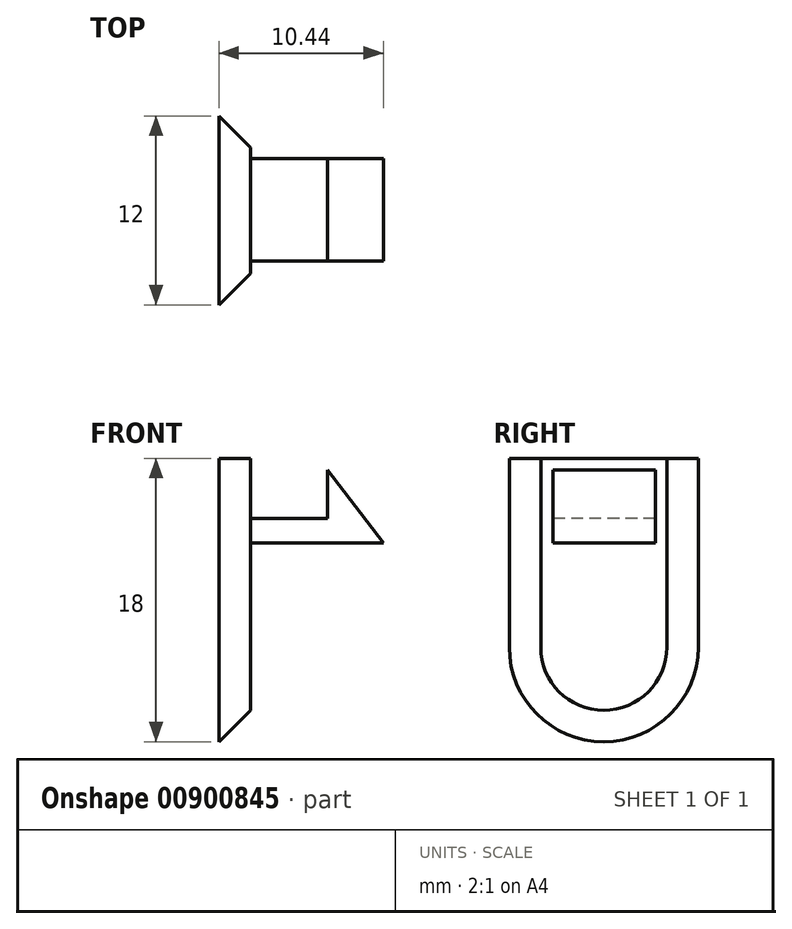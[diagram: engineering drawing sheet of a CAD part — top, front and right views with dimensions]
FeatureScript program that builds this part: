
annotation { "Feature Type Name" : "Feature", "Feature Type Description" : "" }
export const myFeature = defineFeature(function(context is Context, id is Id, definition is map)
    precondition{}
    {
        {
            var Q0;
            Q0=qCreatedBy(makeId("Right.planeOp"),FACE);
            var sketch = newSketch(context, id + "F0", { "sketchPlane" : qUnion([Q0])});
            skLineSegment(sketch, "E0.bottom", {"start": v(6, 9) * mm, "end": v(-6, 9) * mm});
            skLineSegment(sketch, "E0.top", {"start": v(6, -9) * mm, "end": v(-6, -9) * mm});
            skLineSegment(sketch, "E0.left", {"start": v(6, 9) * mm, "end": v(6, -9) * mm});
            skLineSegment(sketch, "E0.right", {"start": v(-6, 9) * mm, "end": v(-6, -9) * mm});
            skPoint(sketch, "E0.middle", {"position": v(0, 0) * mm});
            skLineSegment(sketch, "E1", {"start": v(-45.32, 0) * mm, "end": v(56.37, 0) * mm, "construction": true});
            skLineSegment(sketch, "E2", {"start": v(0, 55.34) * mm, "end": v(0, -57.03) * mm, "construction": true});
            skSolve(sketch);
        }
        {
            var Q0;
            Q0=makeQuery(id+"F0.imprint","IMPRINT",FACE,{"disambiguationData":[TD([[makeQuery(id+"F0.imprint","IMPRINT",EDGE,{"derivedFrom":sQuery(id+"F0.wireOp",EDGE,"E0.bottom")}),1.0]])]});
            extrude(context, id + "F1", {"entities" : qUnion([Q0]), "depth" : 2 * mm, "offsetDistance" : 25 * mm});
        }
        {
            var Q0;
            Q0=makeQuery(id+"F1.opExtrude","CAP_FACE",FACE,{"disambiguationData":[OSD([sQuery(id+"F0.wireOp",EDGE,"E0.bottom"),sQuery(id+"F0.wireOp",EDGE,"E0.top"),sQuery(id+"F0.wireOp",EDGE,"E0.left"),sQuery(id+"F0.wireOp",EDGE,"E0.right")])],"isStart":false});
            var sketch = newSketch(context, id + "F2", { "sketchPlane" : qUnion([Q0])});
            skLineSegment(sketch, "E3.bottom", {"start": v(-4.5, 9) * mm, "end": v(4.5, 9) * mm});
            skLineSegment(sketch, "E3.top", {"start": v(-4.5, -7) * mm, "end": v(4.5, -7) * mm});
            skLineSegment(sketch, "E3.left", {"start": v(-4.5, 9) * mm, "end": v(-4.5, -7) * mm});
            skLineSegment(sketch, "E3.right", {"start": v(4.5, 9) * mm, "end": v(4.5, -7) * mm});
            skSolve(sketch);
        }
        {
            var Q0;
            Q0=makeQuery(id+"F1.opExtrude","SWEPT_EDGE",EDGE,{"disambiguationData":[OSD([sQuery(id+"F0.wireOp",EDGE,"E0.top"),sQuery(id+"F0.wireOp",EDGE,"E0.left")])]});
            var Q1;
            Q1=makeQuery(id+"F1.opExtrude","SWEPT_EDGE",EDGE,{"disambiguationData":[OSD([sQuery(id+"F0.wireOp",EDGE,"E0.top"),sQuery(id+"F0.wireOp",EDGE,"E0.right")])]});
            fillet(context, id + "F3", {"entities" : qUnion([Q0, Q1]), "radius" : 6 * mm, "tangentPropagation" : true, "allowEdgeOverflow" : false});
        }
        {
            var Q0;
            {var subQ0=sQuery(id+"F0.wireOp",EDGE,"E0.left");var subQ1=sQuery(id+"F0.wireOp",EDGE,"E0.top");Q0=makeQuery(id+"F3.opFillet","BLEND_EDGE",EDGE,{"blendedFrom":[makeQuery(id+"F1.opExtrude","SWEPT_EDGE",EDGE,{"disambiguationData":[OSD([subQ1,subQ0])]}),makeQuery(id+"F1.opExtrude","CAP_FACE",FACE,{"disambiguationData":[OSD([sQuery(id+"F0.wireOp",EDGE,"E0.bottom"),subQ1,subQ0,sQuery(id+"F0.wireOp",EDGE,"E0.right")])],"isStart":false})],"blendedInto":[makeQuery(id+"F1.opExtrude","CAP_FACE",FACE,{"disambiguationData":[OSD([sQuery(id+"F0.wireOp",EDGE,"E0.bottom"),subQ1,subQ0,sQuery(id+"F0.wireOp",EDGE,"E0.right")])],"isStart":false})]});}
            var Q1;
            Q1=makeQuery(id+"F1.opExtrude","CAP_EDGE",EDGE,{"disambiguationData":[OSD([sQuery(id+"F0.wireOp",EDGE,"E0.right")])],"isStart":false});
            chamfer(context, id + "F4", {"entities" : qUnion([Q0, Q1]), "width" : 2 * mm, "tangentPropagation" : true});
        }
        {
            var Q0;
            Q0=makeQuery(id+"F2.imprint","IMPRINT",FACE,{"disambiguationData":[TD([[makeQuery(id+"F2.imprint","IMPRINT",EDGE,{"derivedFrom":sQuery(id+"F2.wireOp",EDGE,"E3.bottom")}),1.0]])]});
            var sketch = newSketch(context, id + "F5", { "sketchPlane" : qUnion([Q0])});
            skLineSegment(sketch, "E4.bottom", {"start": v(-3.23, 8.25) * mm, "end": v(3.28, 8.25) * mm});
            skLineSegment(sketch, "E4.top", {"start": v(-3.23, 3.63) * mm, "end": v(3.28, 3.63) * mm});
            skLineSegment(sketch, "E4.left", {"start": v(-3.23, 8.25) * mm, "end": v(-3.23, 3.63) * mm});
            skLineSegment(sketch, "E4.right", {"start": v(3.28, 8.25) * mm, "end": v(3.28, 3.63) * mm});
            skPoint(sketch, "E4.middle", {"position": v(0.03, 5.94) * mm});
            skSolve(sketch);
        }
        {
            var Q0;
            Q0 = qSketchRegion(id + "F5", true);
            extrude(context, id + "F6", {"entities" : qUnion([Q0]), "operationType" : NewBodyOperationType.ADD, "depth" : 10 * mm, "offsetDistance" : 25 * mm});
        }
        {
            var Q0;
            Q0=makeQuery(id+"F6.opExtrude","SWEPT_FACE",FACE,{"disambiguationData":[OSD([sQuery(id+"F5.wireOp",EDGE,"E4.left")])]});
            var sketch = newSketch(context, id + "F7", { "sketchPlane" : qUnion([Q0])});
            skLineSegment(sketch, "E5.bottom", {"start": v(2, 8.25) * mm, "end": v(6.9, 8.25) * mm});
            skLineSegment(sketch, "E5.top", {"start": v(2, 5.19) * mm, "end": v(6.9, 5.19) * mm});
            skLineSegment(sketch, "E5.left", {"start": v(2, 8.25) * mm, "end": v(2, 5.19) * mm});
            skLineSegment(sketch, "E5.right", {"start": v(6.9, 8.25) * mm, "end": v(6.9, 5.19) * mm});
            skLineSegment(sketch, "E6", {"start": v(6.9, 8.25) * mm, "end": v(10.91, 3.02) * mm});
            skLineSegment(sketch, "E7", {"start": v(10.91, 3.02) * mm, "end": v(13.64, 3.02) * mm});
            skLineSegment(sketch, "E8", {"start": v(13.64, 3.02) * mm, "end": v(12.89, 9.03) * mm});
            skLineSegment(sketch, "E9", {"start": v(12.89, 9.03) * mm, "end": v(6.9, 9.03) * mm});
            skLineSegment(sketch, "E10", {"start": v(6.9, 9.03) * mm, "end": v(6.9, 8.25) * mm});
            skSolve(sketch);
        }
        {
            var Q0;
            Q0 = qSketchRegion(id + "F7", true);
            extrude(context, id + "F8", {"entities" : qUnion([Q0]), "operationType" : NewBodyOperationType.REMOVE, "oppositeDirection" : true, "depth" : 25 * mm, "offsetDistance" : 25 * mm});
        }
    });
